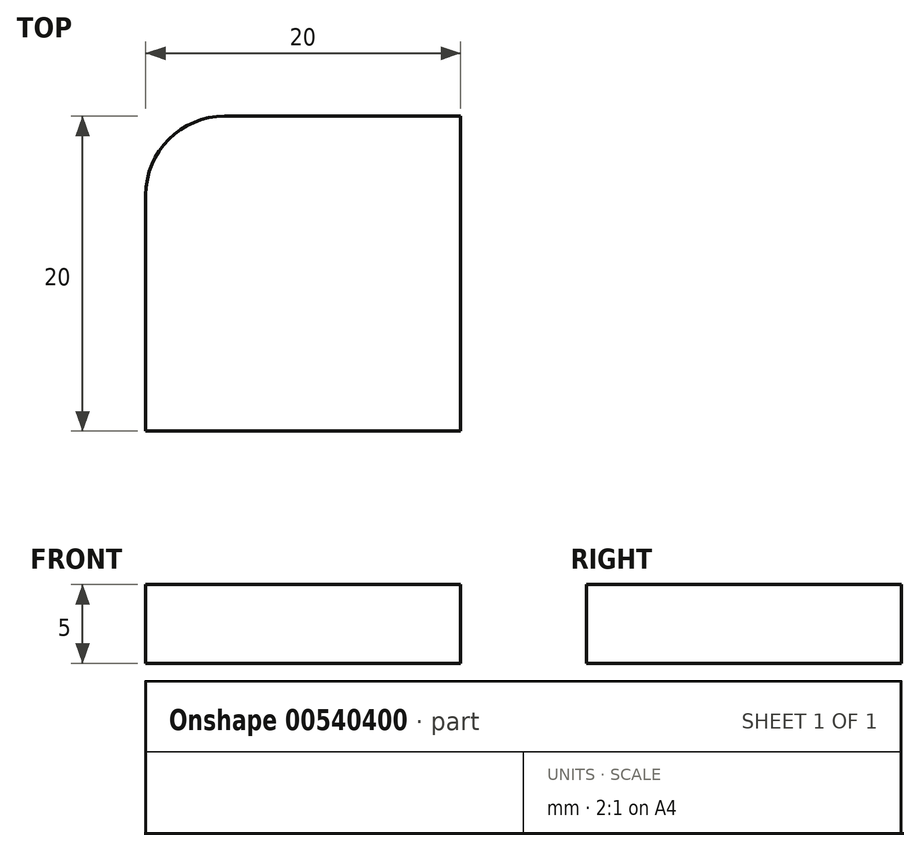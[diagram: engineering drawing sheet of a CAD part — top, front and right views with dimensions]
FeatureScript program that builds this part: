
annotation { "Feature Type Name" : "Feature", "Feature Type Description" : "" }
export const myFeature = defineFeature(function(context is Context, id is Id, definition is map)
    precondition{}
    {
        {
            var Q0;
            Q0=qCreatedBy(makeId("Top.planeOp"),FACE);
            var sketch = newSketch(context, id + "F0", { "sketchPlane" : qUnion([Q0])});
            skLineSegment(sketch, "E0.bottom", {"start": v(-6.33, 16.6) * mm, "end": v(8.67, 16.6) * mm});
            skLineSegment(sketch, "E0.top", {"start": v(-11.33, -3.4) * mm, "end": v(8.67, -3.4) * mm});
            skLineSegment(sketch, "E0.left", {"start": v(-11.33, 11.6) * mm, "end": v(-11.33, -3.4) * mm});
            skLineSegment(sketch, "E0.right", {"start": v(8.67, 16.6) * mm, "end": v(8.67, -3.4) * mm});
            skPoint(sketch, "E1.visualSharp", {"position": v(-11.33, 16.6) * mm});
            skArc(sketch, "E1.filletArc", {"start": v(-6.33, 16.6) * mm, "mid": v(-9.86, 15.14) * mm, "end": v(-11.33, 11.6) * mm});
            skSolve(sketch);
        }
        {
            var Q0;
            Q0=makeQuery(id+"F0.imprint","IMPRINT",FACE,{"disambiguationData":[TD([[makeQuery(id+"F0.imprint","IMPRINT",EDGE,{"derivedFrom":sQuery(id+"F0.wireOp",EDGE,"E0.bottom")}),-1.0]])]});
            extrude(context, id + "F1", {"entities" : qUnion([Q0]), "depth" : 5 * mm, "offsetDistance" : 25 * mm});
        }
    });
